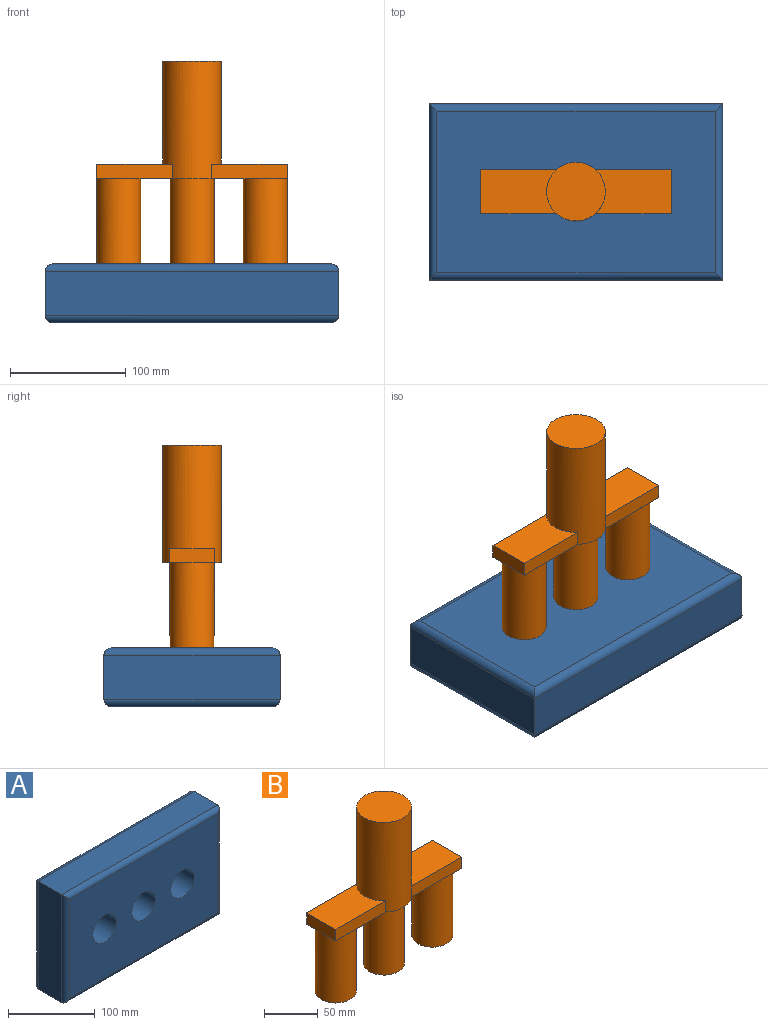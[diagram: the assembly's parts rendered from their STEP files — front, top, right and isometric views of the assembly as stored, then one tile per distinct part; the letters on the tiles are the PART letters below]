
ASSEMBLY  parts=2 mates=1
PART A: 17 faces, bbox 254x50.8x152.4 mm
  f0: plane 254x38.1mm, normal (0,0,-1), area 9677.4mm2, adj f1,f6,f9,f13
  f1: plane 152.4x38.1mm, normal (1,0,0), area 5806.4mm2, adj f0,f2,f10,f14
  f2: plane 254x38.1mm, normal (0,0,1), area 9677.4mm2, adj f1,f6,f12,f16
  f3: cylinder r=19.05mm len=50.8mm, axis (0,1,0), area 6080.5mm2, adj f7,f8
  f4: cylinder r=19.05mm len=50.8mm, axis (0,1,0), area 6080.5mm2, adj f7,f8
  f5: cylinder r=19.05mm len=50.8mm, axis (0,1,0), area 6080.5mm2, adj f7,f8
  f6: plane 152.4x38.1mm, normal (-1,0,0), area 5806.4mm2, adj f0,f2,f11,f15
  f7: plane 241.3x139.7mm, normal (0,-1,0), area 30289.3mm2, adj f3,f4,f5,f13,f14,f15,f16
  f8: plane 241.3x139.7mm, normal (0,1,0), area 30289.3mm2, adj f3,f4,f5,f9,f10,f11,f12
  f9: cylinder r=6.35mm len=254mm, axis (1,0,0), area 2487.5mm2, adj f0,f8,f10,f11
  f10: cylinder r=6.35mm len=152.4mm, axis (0,0,1), area 1474.1mm2, adj f1,f8,f9,f12
  f11: cylinder r=6.35mm len=152.4mm, axis (0,0,-1), area 1474.1mm2, adj f6,f8,f9,f12
  f12: cylinder r=6.35mm len=254mm, axis (-1,0,0), area 2487.5mm2, adj f2,f8,f10,f11
  f13: cylinder r=6.35mm len=254mm, axis (-1,0,0), area 2487.5mm2, adj f0,f7,f14,f15
  f14: cylinder r=6.35mm len=152.4mm, axis (0,0,-1), area 1474.1mm2, adj f1,f7,f13,f16
  f15: cylinder r=6.35mm len=152.4mm, axis (0,0,1), area 1474.1mm2, adj f6,f7,f13,f16
  f16: cylinder r=6.35mm len=254mm, axis (1,0,0), area 2487.5mm2, adj f2,f7,f14,f15
PART B: 21 faces, bbox 165.1x50.8x177.8 mm
  f0: plane 65.75x12.7mm, normal (0,1,0), area 835mm2, adj f4,f6,f8,f10,f19
  f1: plane 65.75x12.7mm, normal (0,1,0), area 835mm2, adj f5,f8,f9,f11,f19
  f2: plane 65.75x12.7mm, normal (0,-1,0), area 835mm2, adj f4,f7,f8,f10,f19
  f3: plane 65.75x12.7mm, normal (0,-1,0), area 835mm2, adj f8,f9,f11,f12,f19
  f4: plane 65.75x38.1mm, normal (0,0,1), area 2278mm2, adj f0,f2,f10,f19
  f5: plane 19.05x19.05mm, normal (0,0,-1), area 77.9mm2, adj f1,f9,f17
  f6: plane 19.05x19.05mm, normal (0,0,-1), area 77.9mm2, adj f0,f10,f15
  f7: plane 19.05x19.05mm, normal (0,0,-1), area 77.9mm2, adj f2,f10,f15
  f8: plane 127x50.8mm, normal (0,0,-1), area 2851mm2, adj f0,f1,f2,f3,f13,f15,f17,f19
  f9: plane 38.1x12.7mm, normal (1,0,0), area 483.9mm2, adj f1,f3,f5,f11,f12
  f10: plane 38.1x12.7mm, normal (-1,0,0), area 483.9mm2, adj f0,f2,f4,f6,f7
  f11: plane 65.75x38.1mm, normal (0,0,1), area 2278mm2, adj f1,f3,f9,f19
  f12: plane 19.05x19.05mm, normal (0,0,-1), area 77.9mm2, adj f3,f9,f17
  f13: cylinder r=19.05mm len=76.2mm, axis (0,0,1), area 9120.7mm2, adj f8,f14
  f14: plane 38.1x38.1mm, normal (0,0,-1), area 1140.1mm2, adj f13
  f15: cylinder r=19.05mm len=76.2mm, axis (0,0,1), area 9120.7mm2, adj f6,f7,f8,f16
  f16: plane 38.1x38.1mm, normal (0,0,-1), area 1140.1mm2, adj f15
  f17: cylinder r=19.05mm len=76.2mm, axis (0,0,1), area 9120.7mm2, adj f5,f8,f12,f18
  f18: plane 38.1x38.1mm, normal (0,0,-1), area 1140.1mm2, adj f17
  f19: cylinder r=25.4mm len=101.6mm, axis (0,0,-1), area 15120.4mm2, adj f0,f1,f2,f3,f4,f8,f11,f20
  f20: plane 50.8x50.8mm, normal (0,0,1), area 2026.8mm2, adj f19
PLACE A rot(axis=(1,0,0),90deg) t=(-65.55,175.4,-366.49)mm
PLACE B t=(-65.55,175.4,-292.67)mm
MATE slider A.f5 <-> B.f13  axis (0,0,-1) through (-65.55,175.4,-417.29)mm
